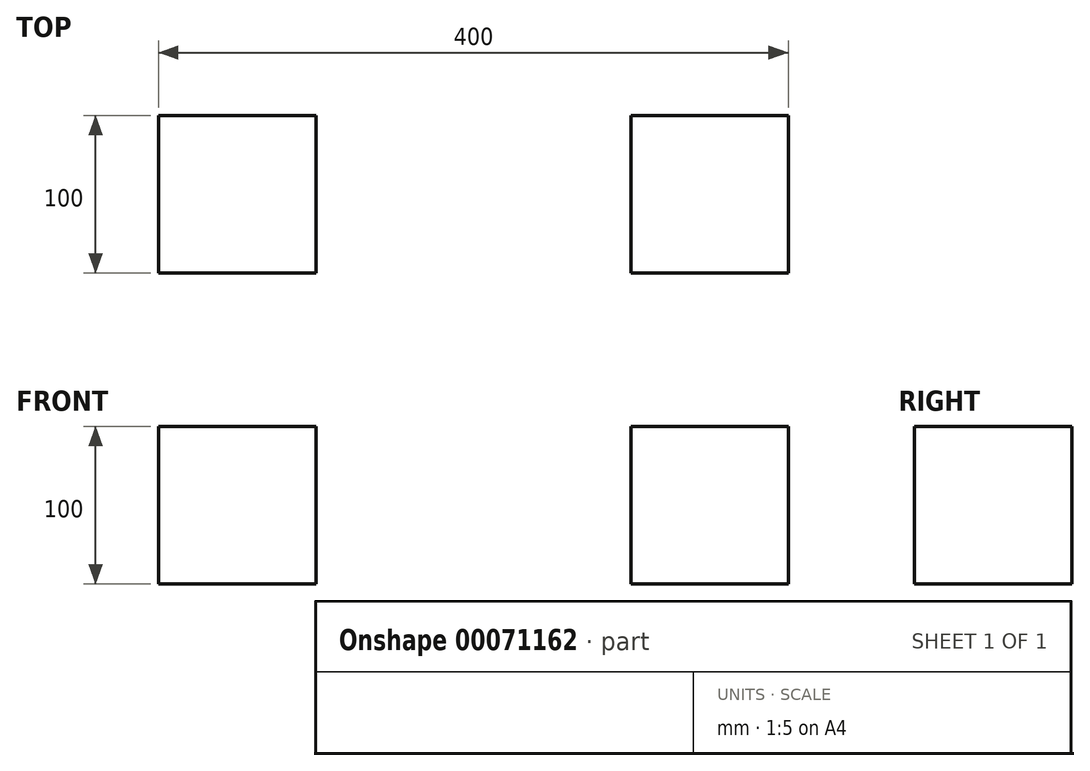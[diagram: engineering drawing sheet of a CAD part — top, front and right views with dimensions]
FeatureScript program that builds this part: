
annotation { "Feature Type Name" : "Feature", "Feature Type Description" : "" }
export const myFeature = defineFeature(function(context is Context, id is Id, definition is map)
    precondition{}
    {
        {
            var Q0;
            Q0=qCreatedBy(makeId("Front.planeOp"),FACE);
            var sketch = newSketch(context, id + "F0", { "sketchPlane" : qUnion([Q0])});
            skLineSegment(sketch, "E0.bottom", {"start": v(0, 0) * mm, "end": v(100, 0) * mm});
            skLineSegment(sketch, "E0.top", {"start": v(0, 100) * mm, "end": v(100, 100) * mm});
            skLineSegment(sketch, "E0.left", {"start": v(0, 0) * mm, "end": v(0, 100) * mm});
            skLineSegment(sketch, "E0.right", {"start": v(100, 0) * mm, "end": v(100, 100) * mm});
            skSolve(sketch);
        }
        {
            var Q0;
            Q0 = qSketchRegion(id + "F0", true);
            extrude(context, id + "F1", {"entities" : qUnion([Q0]), "depth" : 100 * mm});
        }
        {
            var Q0;
            Q0=makeQuery(id+"F1.opExtrude","SWEPT_BODY",BODY,{"disambiguationData":[OSD([sQuery(id+"F0.wireOp",EDGE,"E0.bottom"),sQuery(id+"F0.wireOp",EDGE,"E0.top"),sQuery(id+"F0.wireOp",EDGE,"E0.left"),sQuery(id+"F0.wireOp",EDGE,"E0.right")])]});
            transform(context, id + "F2", {"entities" : qUnion([Q0]), "transformType" : TransformType.TRANSLATION_3D, "dx" : 300 * mm, "dy" : 0 * mm, "dz" : 0 * mm, "makeCopy" : true});
        }
    });
